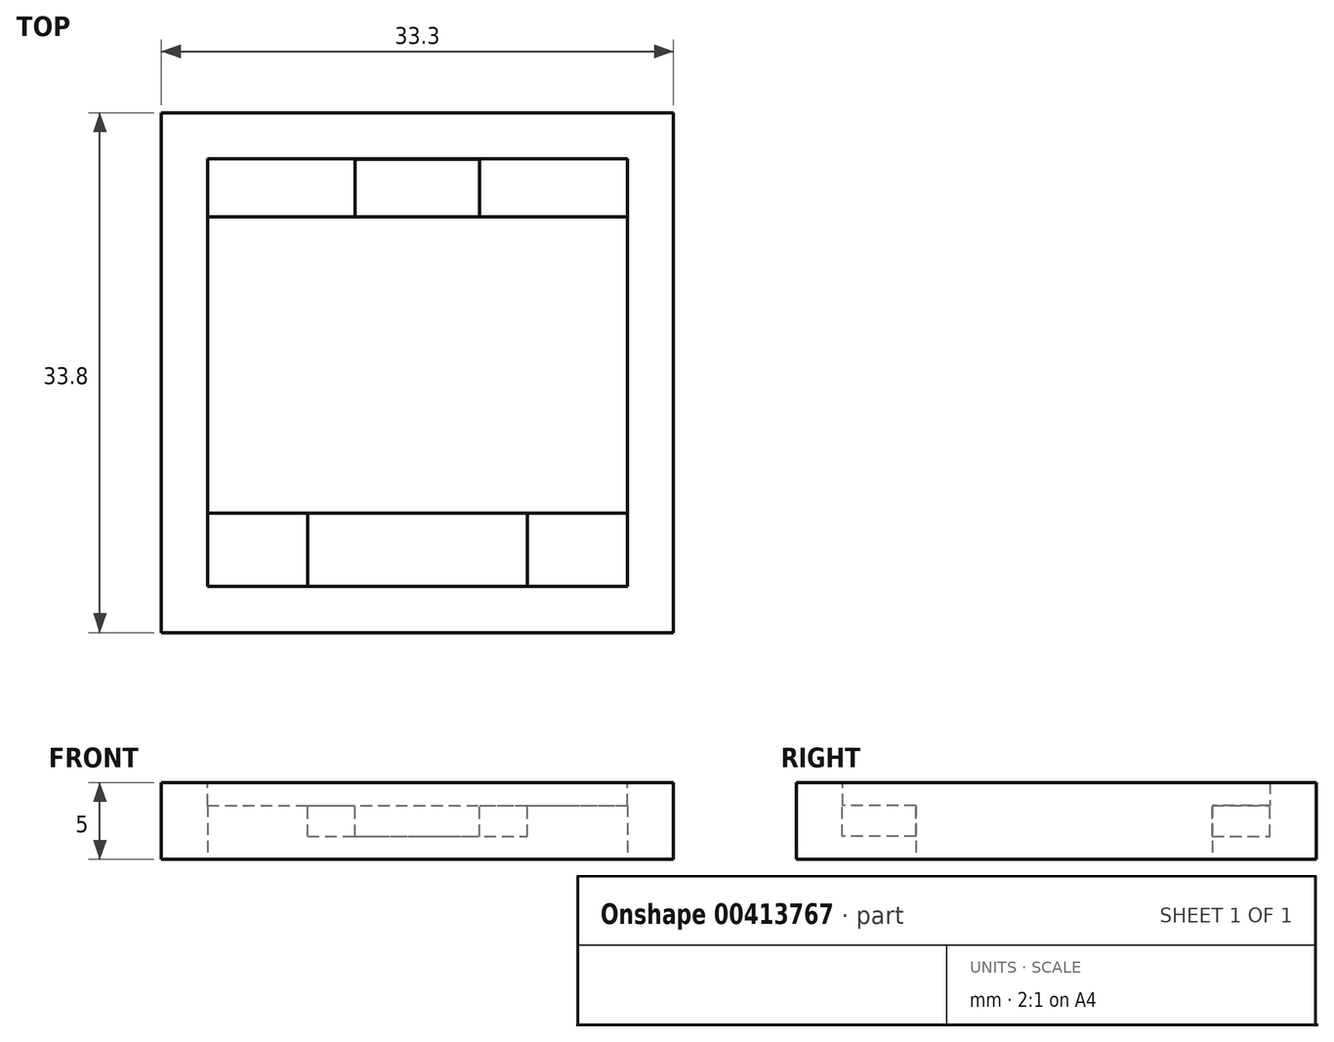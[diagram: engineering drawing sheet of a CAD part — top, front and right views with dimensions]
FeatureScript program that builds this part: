
annotation { "Feature Type Name" : "Feature", "Feature Type Description" : "" }
export const myFeature = defineFeature(function(context is Context, id is Id, definition is map)
    precondition{}
    {
        {
            var Q0;
            Q0=qCreatedBy(makeId("Top.planeOp"),FACE);
            var sketch = newSketch(context, id + "F0", { "sketchPlane" : qUnion([Q0])});
            skLineSegment(sketch, "E0.bottom", {"start": v(-13.65, 13.9) * mm, "end": v(13.65, 13.9) * mm});
            skLineSegment(sketch, "E0.top", {"start": v(-13.65, -13.9) * mm, "end": v(13.65, -13.9) * mm});
            skLineSegment(sketch, "E0.left", {"start": v(-13.65, 13.9) * mm, "end": v(-13.65, -13.9) * mm});
            skLineSegment(sketch, "E0.right", {"start": v(13.65, 13.9) * mm, "end": v(13.65, -13.9) * mm});
            skPoint(sketch, "E0.middle", {"position": v(0, 0) * mm});
            skLineSegment(sketch, "E1.0", {"start": v(16.65, 16.9) * mm, "end": v(16.65, -16.9) * mm});
            skLineSegment(sketch, "E1.1", {"start": v(-16.65, 16.9) * mm, "end": v(16.65, 16.9) * mm});
            skLineSegment(sketch, "E1.2", {"start": v(-16.65, 16.9) * mm, "end": v(-16.65, -16.9) * mm});
            skLineSegment(sketch, "E1.3", {"start": v(-16.65, -16.9) * mm, "end": v(16.65, -16.9) * mm});
            skCircle(sketch, "E2", {"center": v(11.65, -11.9) * mm, "radius": 1.75 * mm, "construction": true});
            skCircle(sketch, "E3", {"center": v(11.65, 11.9) * mm, "radius": 1.75 * mm, "construction": true});
            skCircle(sketch, "E4", {"center": v(-11.65, 11.9) * mm, "radius": 1.75 * mm, "construction": true});
            skCircle(sketch, "E5", {"center": v(-11.65, -11.9) * mm, "radius": 1.75 * mm, "construction": true});
            skLineSegment(sketch, "E6.bottom", {"start": v(-13.65, 10.15) * mm, "end": v(13.65, 10.15) * mm});
            skLineSegment(sketch, "E6.top", {"start": v(-13.65, -9.13) * mm, "end": v(13.65, -9.13) * mm});
            skLineSegment(sketch, "E6.left", {"start": v(-13.65, 10.15) * mm, "end": v(-13.65, -9.13) * mm});
            skLineSegment(sketch, "E6.right", {"start": v(13.65, 10.15) * mm, "end": v(13.65, -9.13) * mm});
            skSolve(sketch);
        }
        {
            var Q0;
            {var subQ4=sQuery(id+"F0.wireOp",EDGE,"E0.bottom");Q0=makeQuery(id+"F0.imprint","IMPRINT",FACE,{"disambiguationData":[TD([[makeQuery(id+"F0.imprint","IMPRINT",EDGE,{"derivedFrom":subQ4}),1.0]])]});}
            extrude(context, id + "F1", {"entities" : qUnion([Q0]), "depth" : 5 * mm, "offsetDistance" : 25 * mm});
        }
        {
            var Q0;
            Q0=qCreatedBy(makeId("Top.planeOp"),FACE);
            var sketch = newSketch(context, id + "F2", { "sketchPlane" : qUnion([Q0])});
            skLineSegment(sketch, "E7.bottom", {"start": v(-13.65, 13.9) * mm, "end": v(13.65, 13.9) * mm});
            skLineSegment(sketch, "E7.top", {"start": v(-13.65, -13.9) * mm, "end": v(13.65, -13.9) * mm});
            skLineSegment(sketch, "E7.left", {"start": v(-13.65, 13.9) * mm, "end": v(-13.65, -13.9) * mm});
            skLineSegment(sketch, "E7.right", {"start": v(13.65, 13.9) * mm, "end": v(13.65, -13.9) * mm});
            skPoint(sketch, "E7.middle", {"position": v(0, 0) * mm});
            skCircle(sketch, "E8", {"center": v(11.65, -11.9) * mm, "radius": 1.75 * mm, "construction": true});
            skCircle(sketch, "E9", {"center": v(11.65, 11.9) * mm, "radius": 1.75 * mm, "construction": true});
            skCircle(sketch, "E10", {"center": v(-11.65, 11.9) * mm, "radius": 1.75 * mm, "construction": true});
            skCircle(sketch, "E11", {"center": v(-11.65, -11.9) * mm, "radius": 1.75 * mm, "construction": true});
            skLineSegment(sketch, "E12.bottom", {"start": v(-13.65, 10.15) * mm, "end": v(13.65, 10.15) * mm});
            skLineSegment(sketch, "E12.top", {"start": v(-13.65, -9.13) * mm, "end": v(13.65, -9.13) * mm});
            skLineSegment(sketch, "E12.left", {"start": v(-13.65, 10.15) * mm, "end": v(-13.65, -9.13) * mm});
            skLineSegment(sketch, "E12.right", {"start": v(13.65, 10.15) * mm, "end": v(13.65, -9.13) * mm});
            skSolve(sketch);
        }
        {
            var Q0;
            {var subQ0=sQuery(id+"F2.wireOp",EDGE,"E7.bottom");Q0=makeQuery(id+"F2.imprint","IMPRINT",FACE,{"disambiguationData":[TD([[makeQuery(id+"F2.imprint","IMPRINT",EDGE,{"derivedFrom":subQ0}),-1.0]])]});}
            var Q1;
            {var subQ0=sQuery(id+"F2.wireOp",EDGE,"E7.top");Q1=makeQuery(id+"F2.imprint","IMPRINT",FACE,{"disambiguationData":[TD([[makeQuery(id+"F2.imprint","IMPRINT",EDGE,{"derivedFrom":subQ0}),1.0]])]});}
            extrude(context, id + "F3", {"entities" : qUnion([Q0, Q1]), "operationType" : NewBodyOperationType.ADD, "depth" : 3.5 * mm, "offsetDistance" : 25 * mm});
        }
        {
            var Q0;
            Q0=qCreatedBy(makeId("Top.planeOp"),FACE);
            cPlane(context, id + "F4", {"entities" : qUnion([Q0]), "cplaneType" : CPlaneType.OFFSET, "offset" : 3.5 * mm, "width" : 150 * mm, "height" : 150 * mm});
        }
        {
            var Q0;
            Q0=qCreatedBy(id+"F4.planeOp",FACE);
            var sketch = newSketch(context, id + "F5", { "sketchPlane" : qUnion([Q0])});
            skLineSegment(sketch, "E13", {"start": v(-4.05, 27.74) * mm, "end": v(-4.05, -4.9) * mm, "construction": true});
            skLineSegment(sketch, "E14", {"start": v(4.05, 21.83) * mm, "end": v(4.05, 6.4) * mm, "construction": true});
            skLineSegment(sketch, "E15", {"start": v(-7.15, -5.52) * mm, "end": v(-7.15, -18.12) * mm, "construction": true});
            skLineSegment(sketch, "E16", {"start": v(7.15, -5.91) * mm, "end": v(7.15, -17.84) * mm, "construction": true});
            skLineSegment(sketch, "E17.bottom", {"start": v(-4.05, 10.14) * mm, "end": v(4.05, 10.14) * mm});
            skLineSegment(sketch, "E17.top", {"start": v(-4.05, 13.9) * mm, "end": v(4.05, 13.9) * mm});
            skLineSegment(sketch, "E17.left", {"start": v(-4.05, 10.14) * mm, "end": v(-4.05, 13.9) * mm});
            skLineSegment(sketch, "E17.right", {"start": v(4.05, 10.14) * mm, "end": v(4.05, 13.9) * mm});
            skLineSegment(sketch, "E18.bottom", {"start": v(-7.15, -9.11) * mm, "end": v(7.15, -9.11) * mm});
            skLineSegment(sketch, "E18.top", {"start": v(-7.15, -13.92) * mm, "end": v(7.15, -13.92) * mm});
            skLineSegment(sketch, "E18.left", {"start": v(-7.15, -9.11) * mm, "end": v(-7.15, -13.92) * mm});
            skLineSegment(sketch, "E18.right", {"start": v(7.15, -9.11) * mm, "end": v(7.15, -13.92) * mm});
            skSolve(sketch);
        }
        {
            var Q0;
            Q0 = qSketchRegion(id + "F5", true);
            extrude(context, id + "F6", {"entities" : qUnion([Q0]), "operationType" : NewBodyOperationType.REMOVE, "oppositeDirection" : true, "depth" : 2 * mm, "offsetDistance" : 25 * mm});
        }
    });
